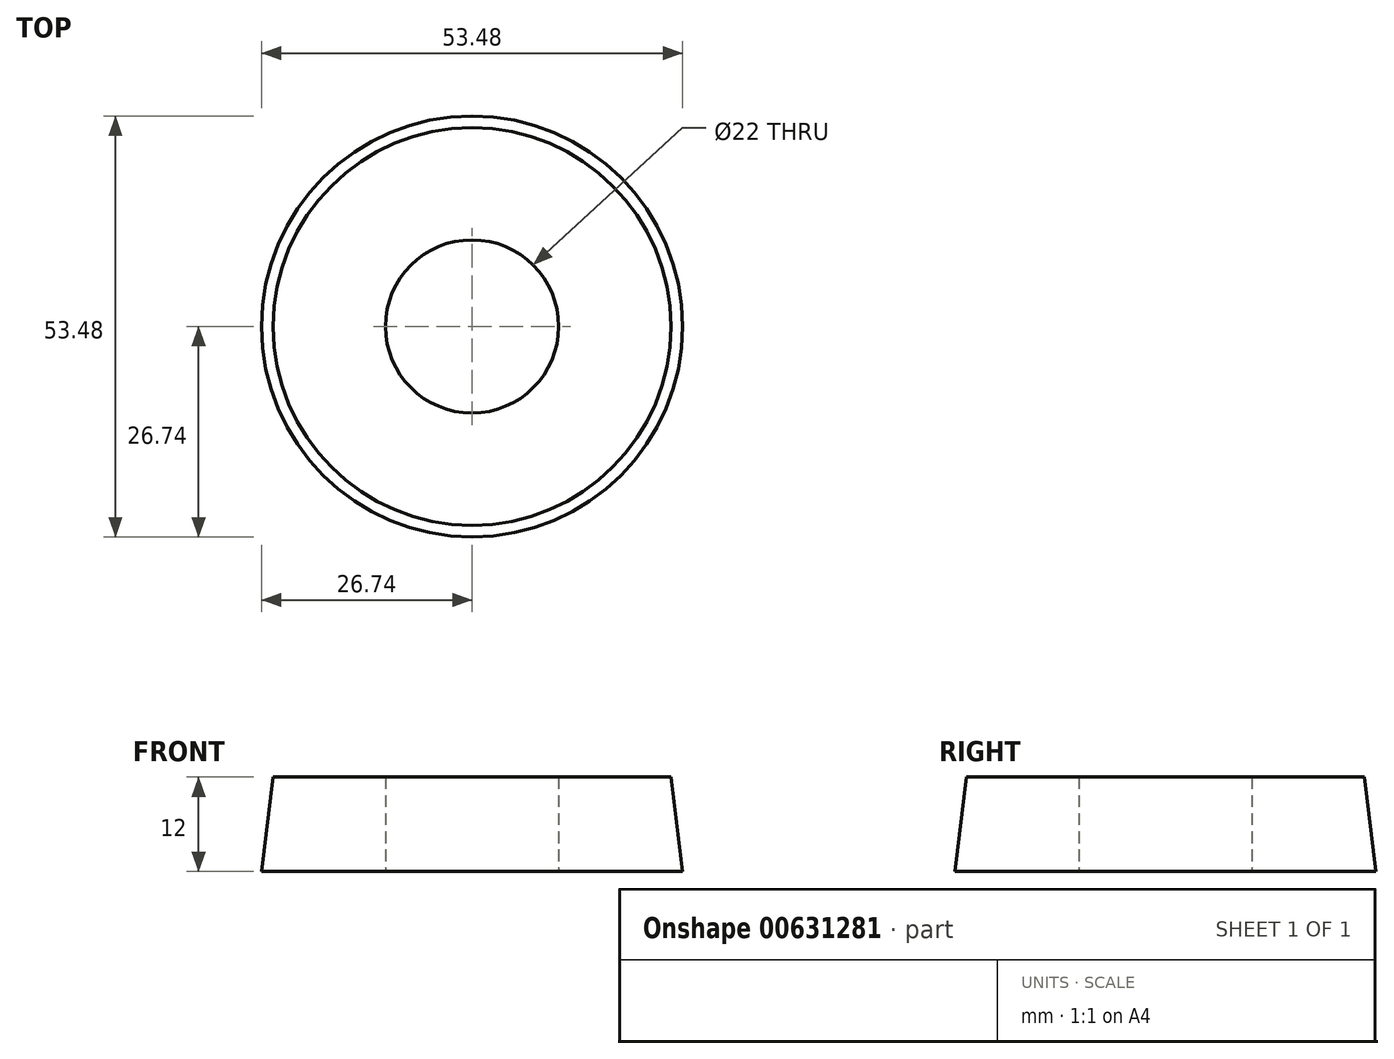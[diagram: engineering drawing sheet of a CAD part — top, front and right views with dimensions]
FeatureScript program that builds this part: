
annotation { "Feature Type Name" : "Feature", "Feature Type Description" : "" }
export const myFeature = defineFeature(function(context is Context, id is Id, definition is map)
    precondition{}
    {
        {
            var Q0;
            Q0=qCreatedBy(makeId("Top.planeOp"),FACE);
            var sketch = newSketch(context, id + "F0", { "sketchPlane" : qUnion([Q0])});
            skCircle(sketch, "E0", {"center": v(0, 0) * mm, "radius": 11 * mm});
            skCircle(sketch, "E1", {"center": v(0, 0) * mm, "radius": 26 * mm});
            skSolve(sketch);
        }
        {
            var Q0;
            Q0=makeQuery(id+"F0.imprint","IMPRINT",FACE,{"disambiguationData":[TD([[makeQuery(id+"F0.imprint","IMPRINT",EDGE,{"derivedFrom":sQuery(id+"F0.wireOp",EDGE,"E0")}),-1.0]])]});
            var Q1;
            Q1=makeQuery(id+"F0.imprint","IMPRINT",FACE,{"disambiguationData":[TD([[makeQuery(id+"F0.imprint","IMPRINT",EDGE,{"derivedFrom":sQuery(id+"F0.wireOp",EDGE,"E0")}),1.0]])]});
            extrude(context, id + "F1", {"entities" : qUnion([Q0, Q1]), "depth" : 6 * mm, "offsetDistance" : 25 * mm, "hasDraft" : true, "draftAngle" : 7 * degree, "draftPullDirection" : true});
        }
        {
            var Q0;
            Q0=makeQuery(id+"F0.imprint","IMPRINT",FACE,{"disambiguationData":[TD([[makeQuery(id+"F0.imprint","IMPRINT",EDGE,{"derivedFrom":sQuery(id+"F0.wireOp",EDGE,"E0")}),-1.0]])]});
            var Q1;
            Q1=makeQuery(id+"F0.imprint","IMPRINT",FACE,{"disambiguationData":[TD([[makeQuery(id+"F0.imprint","IMPRINT",EDGE,{"derivedFrom":sQuery(id+"F0.wireOp",EDGE,"E0")}),1.0]])]});
            extrude(context, id + "F2", {"entities" : qUnion([Q0, Q1]), "operationType" : NewBodyOperationType.ADD, "oppositeDirection" : true, "depth" : 6 * mm, "offsetDistance" : 25 * mm, "hasDraft" : true, "draftAngle" : 7 * degree});
        }
        {
            var Q0;
            Q0=makeQuery(id+"F0.imprint","IMPRINT",FACE,{"disambiguationData":[TD([[makeQuery(id+"F0.imprint","IMPRINT",EDGE,{"derivedFrom":sQuery(id+"F0.wireOp",EDGE,"E0")}),1.0]])]});
            var Q1;
            Q1=makeQuery(id+"F2.opExtrude","CAP_FACE",FACE,{"disambiguationData":[OSD([sQuery(id+"F0.wireOp",EDGE,"E1")])],"isStart":false});
            extrude(context, id + "F3", {"entities" : qUnion([Q0]), "operationType" : NewBodyOperationType.REMOVE, "endBound" : BoundingType.UP_TO_NEXT, "depth" : 60 * mm, "offsetDistance" : 25 * mm, "hasSecondDirection" : true, "secondDirectionBound" : SecondDirectionBoundingType.UP_TO_SURFACE, "secondDirectionOppositeDirection" : true, "secondDirectionDepth" : 25 * mm, "secondDirectionBoundEntityFace" : qUnion([Q1])});
        }
    });
